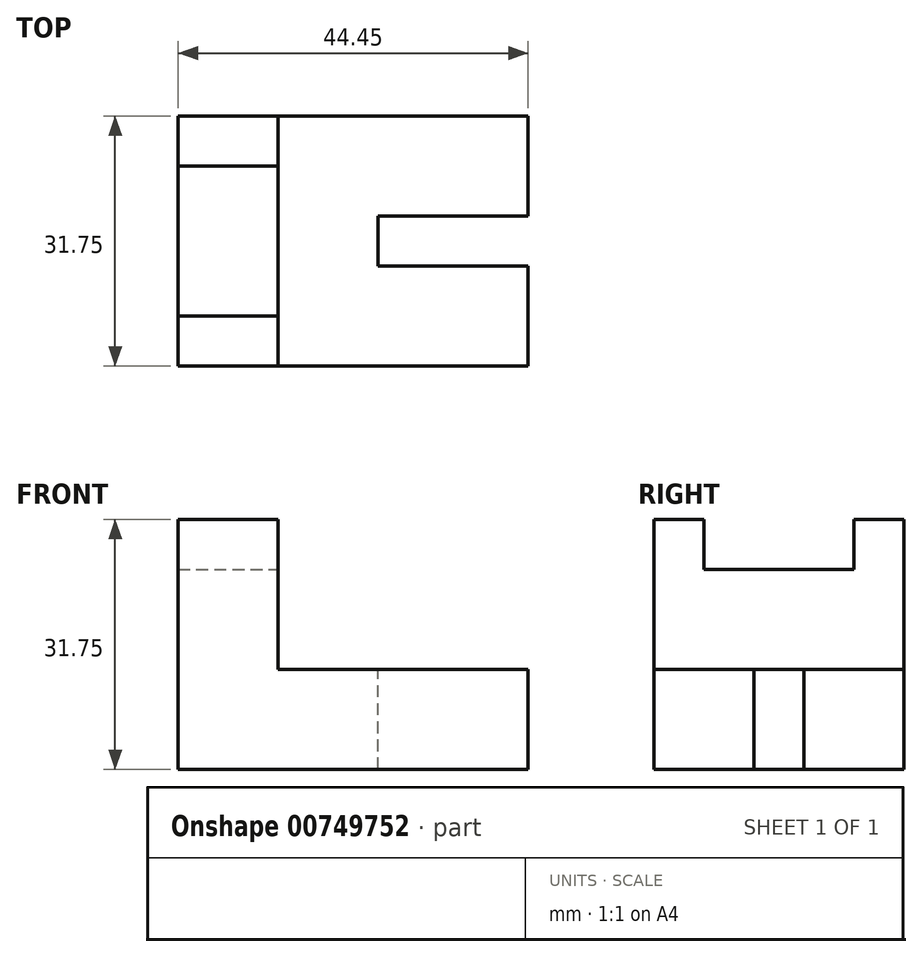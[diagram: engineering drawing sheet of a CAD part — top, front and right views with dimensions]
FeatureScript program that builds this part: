
annotation { "Feature Type Name" : "Feature", "Feature Type Description" : "" }
export const myFeature = defineFeature(function(context is Context, id is Id, definition is map)
    precondition{}
    {
        {
            var Q0;
            Q0=qCreatedBy(makeId("Front.planeOp"),FACE);
            var sketch = newSketch(context, id + "F0", { "sketchPlane" : qUnion([Q0])});
            skLineSegment(sketch, "E0", {"start": v(-18.74, -23.99) * mm, "end": v(25.71, -23.99) * mm});
            skLineSegment(sketch, "E1", {"start": v(-18.74, -23.99) * mm, "end": v(-18.74, 7.76) * mm});
            skLineSegment(sketch, "E2", {"start": v(25.71, -23.99) * mm, "end": v(25.71, -11.29) * mm});
            skLineSegment(sketch, "E3", {"start": v(25.71, -11.29) * mm, "end": v(-6.04, -11.29) * mm});
            skLineSegment(sketch, "E4", {"start": v(-6.04, -11.29) * mm, "end": v(-6.04, 7.76) * mm});
            skLineSegment(sketch, "E5", {"start": v(-6.04, 7.76) * mm, "end": v(-18.74, 7.76) * mm});
            skSolve(sketch);
        }
        {
            var Q0;
            Q0 = qSketchRegion(id + "F0", true);
            extrude(context, id + "F1", {"entities" : qUnion([Q0]), "depth" : 31.75 * mm, "offsetDistance" : 25.4 * mm});
        }
        {
            var Q0;
            Q0=makeQuery(id+"F1.opExtrude","SWEPT_FACE",FACE,{"disambiguationData":[OSD([sQuery(id+"F0.wireOp",EDGE,"E4")])]});
            var sketch = newSketch(context, id + "F2", { "sketchPlane" : qUnion([Q0])});
            skLineSegment(sketch, "E6", {"start": v(-25.4, 7.76) * mm, "end": v(-25.4, 1.41) * mm});
            skLineSegment(sketch, "E7", {"start": v(-25.4, 1.41) * mm, "end": v(-6.35, 1.41) * mm});
            skLineSegment(sketch, "E8", {"start": v(-6.35, 1.41) * mm, "end": v(-6.35, 7.76) * mm});
            skLineSegment(sketch, "E9", {"start": v(-6.35, 7.76) * mm, "end": v(-25.4, 7.76) * mm});
            skSolve(sketch);
        }
        {
            var Q0;
            Q0 = qSketchRegion(id + "F2", true);
            extrude(context, id + "F3", {"entities" : qUnion([Q0]), "operationType" : NewBodyOperationType.REMOVE, "oppositeDirection" : true, "depth" : 25.4 * mm, "offsetDistance" : 25.4 * mm});
        }
        {
            var Q0;
            Q0=makeQuery(id+"F1.opExtrude","SWEPT_FACE",FACE,{"disambiguationData":[OSD([sQuery(id+"F0.wireOp",EDGE,"E3")])]});
            var sketch = newSketch(context, id + "F4", { "sketchPlane" : qUnion([Q0])});
            skLineSegment(sketch, "E10", {"start": v(25.71, -12.7) * mm, "end": v(6.66, -12.7) * mm});
            skLineSegment(sketch, "E11", {"start": v(6.66, -12.7) * mm, "end": v(6.66, -19.05) * mm});
            skLineSegment(sketch, "E12", {"start": v(6.66, -19.05) * mm, "end": v(25.71, -19.05) * mm});
            skLineSegment(sketch, "E13", {"start": v(25.71, -19.05) * mm, "end": v(25.71, -12.7) * mm});
            skSolve(sketch);
        }
        {
            var Q0;
            Q0 = qSketchRegion(id + "F4", true);
            extrude(context, id + "F5", {"entities" : qUnion([Q0]), "operationType" : NewBodyOperationType.REMOVE, "oppositeDirection" : true, "depth" : 25.4 * mm, "offsetDistance" : 25.4 * mm});
        }
    });
